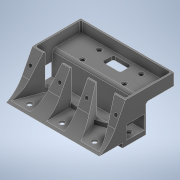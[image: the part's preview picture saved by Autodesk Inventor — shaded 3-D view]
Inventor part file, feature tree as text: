
AUTODESK INVENTOR PART (.ipt)
format: ipt  version: 2021 (Build 250183000, 183)  size: 565,760 bytes
history: native  units: mm
features: other x21, sketch x21, extrude x17, fillet x5, hole x5, chamfer x1
ambient origin geometry x8: Origin, YZ Plane, XZ Plane, XY Plane, X Axis, Y Axis, Z Axis, Center Point
bodies: Body1 (feature_tree)
feature tree (70):
  other  "Sólido1"
  extrude  "Extrusão1"  Depth=50.0mm
  extrude  "Extrusão2"  Depth=1.5mm
  extrude  "Extrusão3"  Depth=20.5mm
  other  "Plano de trabalho1"
  extrude  "Extrusão4"  TaperAngle=0.0deg  [1 undecoded]
  extrude  "Extrusão7"  Depth=1.5mm
  extrude  "Extrusão9"  Depth=50.0mm
  extrude  "Extrusão10"  Depth=1.5mm
  extrude  "Extrusão11"  Depth=25.0mm
  extrude  "Extrusão12"  Depth=5.0mm TaperAngle=0.0deg
  extrude  "Extrusão13"  Depth=19.0mm
  extrude  "Extrusão14"  Depth=1.5mm
  extrude  "Extrusão15"  TaperAngle=0.0deg  [1 undecoded]
  extrude  "Extrusão16"  Depth=14.5mm
  fillet  "Arredondamento2"  Radius=4.85mm
  fillet  "Arredondamento3"  Radius=1.5mm
  hole  "Furo1"  [1 undecoded]
  chamfer  "Chanfro1"  Distance=30.0mm
  extrude  "Extrusão17"  Depth=50.0mm
  fillet  "Arredondamento5"  Radius=2.85mm
  hole  "Furo2"  [1 undecoded]
  hole  "Furo3"  [1 undecoded]
  hole  "Furo4"  [1 undecoded]
  other  "Plano de trabalho2"
  hole  "Furo5"  [1 undecoded]
  extrude  "Extrusão18"  Depth=2.0mm TaperAngle=45.0deg
  extrude  "Extrusão19"  Depth=20.0mm
  fillet  "Arredondamento6"  Radius=12.5mm
  extrude  "Extrusão20"  Depth=50.0mm
  fillet  "Arredondamento7"  Radius=5.0mm
  sketch  "Esboço1"  dims[d0=38.5mm d1=50.0mm]
  sketch  "Esboço2"  dims[d2=100.0mm d3=0.0mm d4=1.5mm]
  other  "Contorno projetado1"
  sketch  "Esboço3"  dims[d5=20.5mm d6=4.633849mm]
  other  "Contorno projetado2"
  sketch  "Esboço4"  dims[d7=10.995574mm d8=0.0mm d9=0.0mm]
  other  "Contorno projetado3"
  other  "Contorno projetado4"
  other  "Contorno projetado5"
  sketch  "Esboço8"  dims[d12=37.0mm d13=0.0mm d14=1.5mm]
  other  "Contorno projetado8"
  sketch  "Esboço11"  dims[d15=19.0mm d16=50.0mm]
  other  "Contorno projetado9"
  sketch  "Esboço12"  dims[d17=19.0mm d19=1.5mm]
  sketch  "Esboço13"  dims[d20=0.0mm d21=0.0mm d32=25.0mm]
  sketch  "Esboço14"  dims[d33=4.85mm d34=0.0mm d37=5.0mm d38=0.0mm]
  sketch  "Esboço15"  dims[d39=4.85mm d40=0.0mm d41=19.0mm]
  sketch  "Esboço16"  dims[d42=15.0mm d43=1.5mm]
  sketch  "Esboço17"  dims[d44=5.0mm d45=0.0mm d46=0.0mm]
  other  "Contorno projetado10"
  sketch  "Esboço18"  dims[d47=14.5mm d48=14.5mm d49=4.85mm d50=0.0mm d51=1.5mm]
  sketch  "Esboço19"  dims[d52=1.5mm d53=4.85mm d54=0.0mm]
  sketch  "Esboço20"  dims[d55=13.0mm d56=30.0mm d57=0.0mm]
  sketch  "Esboço21"  dims[d58=55.0mm d59=50.0mm d60=2.85mm d61=0.0mm]
  sketch  "Esboço22"  dims[d62=1.5mm d63=11.5mm d64=0.0mm]
  other  "Contorno projetado11"
  other  "Contorno projetado12"
  sketch  "Esboço23"  dims[d66=2.85mm d67=1.5mm]
  other  "Contorno projetado13"
  other  "Contorno projetado14"
  other  "Contorno projetado15"
  other  "Contorno projetado16"
  sketch  "Esboço24"  dims[d69=4.5mm d70=5.0mm]
  other  "Contorno projetado17"
  other  "Contorno projetado18"
  sketch  "Esboço26"  dims[d71=5.0mm d72=7.5mm]
  other  "Contorno projetado19"
  other  "Contorno projetado20"
  sketch  "Esboço27"  dims[d73=4.0mm d74=6.0mm d75=4.0mm d76=2.0mm d77=90.0deg d78=5.0mm d79=0.0mm d80=1.0mm d81=2.0mm d82=45.0deg d83=20.0mm d84=12.5mm d85=50.0mm d86=5.0mm d87=0.0mm d88=0.0mm d89=2.0mm d90=8.0mm d91=50.0mm d92=10.0mm d95=4.0mm d96=6.0mm d97=6.0mm d98=2.0mm d99=90.0deg d100=8.0mm d101=20.594885mm d106=4.0mm d107=6.0mm d108=6.0mm d109=2.0mm d110=90.0deg d111=8.0mm d112=20.594885mm d113=4.0mm d114=6.0mm d115=6.0mm d116=2.0mm d117=90.0deg d118=8.0mm d119=20.594885mm d120=35.0mm d121=35.0mm d126=29.0mm d127=43.0mm d128=43.0mm d129=4.0mm d130=4.0mm d131=5.0mm d132=5.0mm d133=10.0mm d134=4.0mm d135=6.0mm d136=4.0mm d137=2.0mm d138=90.0deg d139=5.0mm d140=0.0mm d141=10.0mm d142=0.0mm d143=10.0mm d144=0.0mm d145=4.0mm d146=1.25mm d147=1.25mm d148=10.0mm d149=0.0mm d150=1.5mm]
note: 7 required parameter values undecoded (feature->parameter linkage not recoverable at this tier; creation-order binding heuristic only, values carry confidence <= 0.55)
